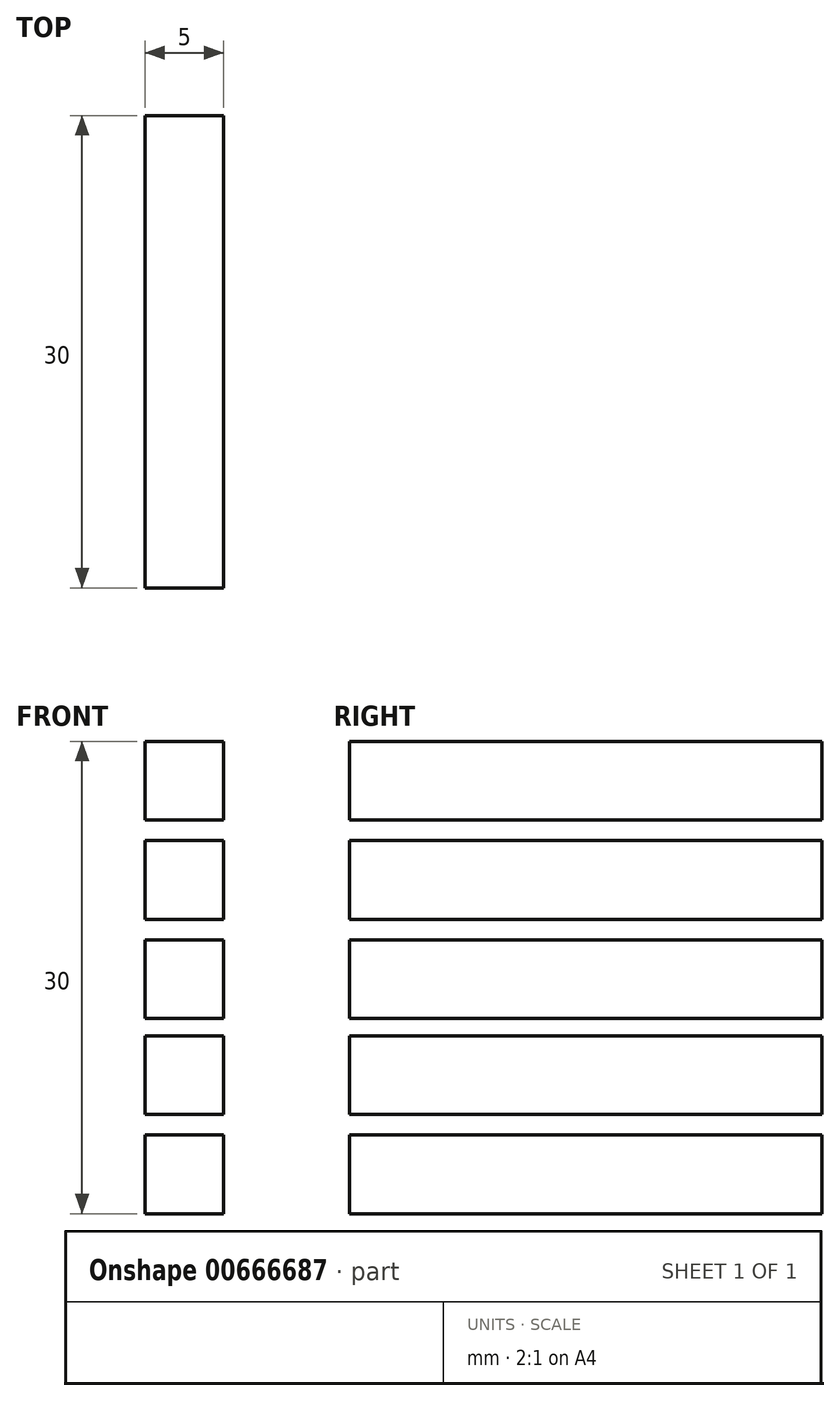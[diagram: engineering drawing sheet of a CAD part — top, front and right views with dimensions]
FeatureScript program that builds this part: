
annotation { "Feature Type Name" : "Feature", "Feature Type Description" : "" }
export const myFeature = defineFeature(function(context is Context, id is Id, definition is map)
    precondition{}
    {
        {
            var Q0;
            Q0=qCreatedBy(makeId("Right.planeOp"),FACE);
            var sketch = newSketch(context, id + "F0", { "sketchPlane" : qUnion([Q0])});
            skLineSegment(sketch, "E0", {"start": v(0, 0) * mm, "end": v(0, -5) * mm});
            skLineSegment(sketch, "E1", {"start": v(0, -30) * mm, "end": v(12.4, -30) * mm});
            skLineSegment(sketch, "E2", {"start": v(30, -30) * mm, "end": v(30, -25) * mm});
            skLineSegment(sketch, "E3", {"start": v(30, 0) * mm, "end": v(23.48, 0) * mm});
            skLineSegment(sketch, "E4", {"start": v(30, -30) * mm, "end": v(17.6, -30) * mm});
            skLineSegment(sketch, "E5.trimOffspring", {"start": v(12.4, -30) * mm, "end": v(0, -30) * mm});
            skLineSegment(sketch, "E6", {"start": v(12, -30) * mm, "end": v(12.4, -30) * mm});
            skLineSegment(sketch, "E7", {"start": v(0, -30) * mm, "end": v(12, -30) * mm});
            skLineSegment(sketch, "E8.trimOffspring", {"start": v(17.6, -30) * mm, "end": v(30, -30) * mm});
            skPoint(sketch, "E9.trimOffspring.start.orphan", {"position": v(15, -30) * mm});
            skLineSegment(sketch, "E10.trimOffspring", {"start": v(23.48, 0) * mm, "end": v(30, 0) * mm});
            skLineSegment(sketch, "E11", {"start": v(0, 0) * mm, "end": v(6.52, 0) * mm});
            skLineSegment(sketch, "E12.0", {"start": v(0, -5) * mm, "end": v(30, -5) * mm});
            skLineSegment(sketch, "E13", {"start": v(0, -30) * mm, "end": v(30, -30) * mm});
            skLineSegment(sketch, "E14.0", {"start": v(0, -25) * mm, "end": v(30, -25) * mm});
            skLineSegment(sketch, "E15.0", {"start": v(0, -6.3) * mm, "end": v(30, -6.3) * mm});
            skLineSegment(sketch, "E16.0", {"start": v(0, -23.7) * mm, "end": v(30, -23.7) * mm});
            skLineSegment(sketch, "E17.0", {"start": v(0, -11.3) * mm, "end": v(30, -11.3) * mm});
            skLineSegment(sketch, "E18.0", {"start": v(0, -18.7) * mm, "end": v(30, -18.7) * mm});
            skLineSegment(sketch, "E19.0", {"start": v(0, -12.6) * mm, "end": v(30, -12.6) * mm});
            skLineSegment(sketch, "E20.0", {"start": v(0, -17.6) * mm, "end": v(30, -17.6) * mm});
            skLineSegment(sketch, "E21.trimOffspring", {"start": v(0, -6.3) * mm, "end": v(0, -11.3) * mm});
            skLineSegment(sketch, "E22.trimOffspring", {"start": v(30, -5) * mm, "end": v(30, 0) * mm});
            skLineSegment(sketch, "E23.trimOffspring", {"start": v(30, -11.3) * mm, "end": v(30, -6.3) * mm});
            skLineSegment(sketch, "E24.trimOffspring", {"start": v(0, -12.6) * mm, "end": v(0, -17.6) * mm});
            skLineSegment(sketch, "E25.trimOffspring", {"start": v(0, -18.7) * mm, "end": v(0, -23.7) * mm});
            skLineSegment(sketch, "E26.trimOffspring", {"start": v(30, -17.6) * mm, "end": v(30, -12.6) * mm});
            skLineSegment(sketch, "E27.trimOffspring", {"start": v(30, -23.7) * mm, "end": v(30, -18.7) * mm});
            skLineSegment(sketch, "E28.trimOffspring", {"start": v(0, -25) * mm, "end": v(0, -30) * mm});
            skPoint(sketch, "E29.trimOffspring.start.orphan", {"position": v(12.4, 0) * mm});
            skLineSegment(sketch, "E30", {"start": v(30, 0) * mm, "end": v(0, 0) * mm});
            skSolve(sketch);
        }
        {
            var Q0;
            {var subQ5=sQuery(id+"F0.wireOp",EDGE,"E2");Q0=makeQuery(id+"F0.imprint","IMPRINT",FACE,{"disambiguationData":[TD([[makeQuery(id+"F0.imprint","IMPRINT",EDGE,{"derivedFrom":subQ5}),1.0]])]});}
            var Q1;
            Q1=makeQuery(id+"F0.imprint","IMPRINT",FACE,{"disambiguationData":[TD([[makeQuery(id+"F0.imprint","IMPRINT",EDGE,{"derivedFrom":sQuery(id+"F0.wireOp",EDGE,"E18.0")}),-1.0]])]});
            var Q2;
            Q2=makeQuery(id+"F0.imprint","IMPRINT",FACE,{"disambiguationData":[TD([[makeQuery(id+"F0.imprint","IMPRINT",EDGE,{"derivedFrom":sQuery(id+"F0.wireOp",EDGE,"E19.0")}),-1.0]])]});
            var Q3;
            Q3=makeQuery(id+"F0.imprint","IMPRINT",FACE,{"disambiguationData":[TD([[makeQuery(id+"F0.imprint","IMPRINT",EDGE,{"derivedFrom":sQuery(id+"F0.wireOp",EDGE,"E15.0")}),-1.0]])]});
            var Q4;
            {var subQ3=sQuery(id+"F0.wireOp",EDGE,"E0");Q4=makeQuery(id+"F0.imprint","IMPRINT",FACE,{"disambiguationData":[TD([[makeQuery(id+"F0.imprint","IMPRINT",EDGE,{"derivedFrom":subQ3}),1.0]])]});}
            extrude(context, id + "F1", {"entities" : qUnion([Q0, Q1, Q2, Q3, Q4]), "depth" : 5 * mm, "offsetDistance" : 25 * mm});
        }
    });
